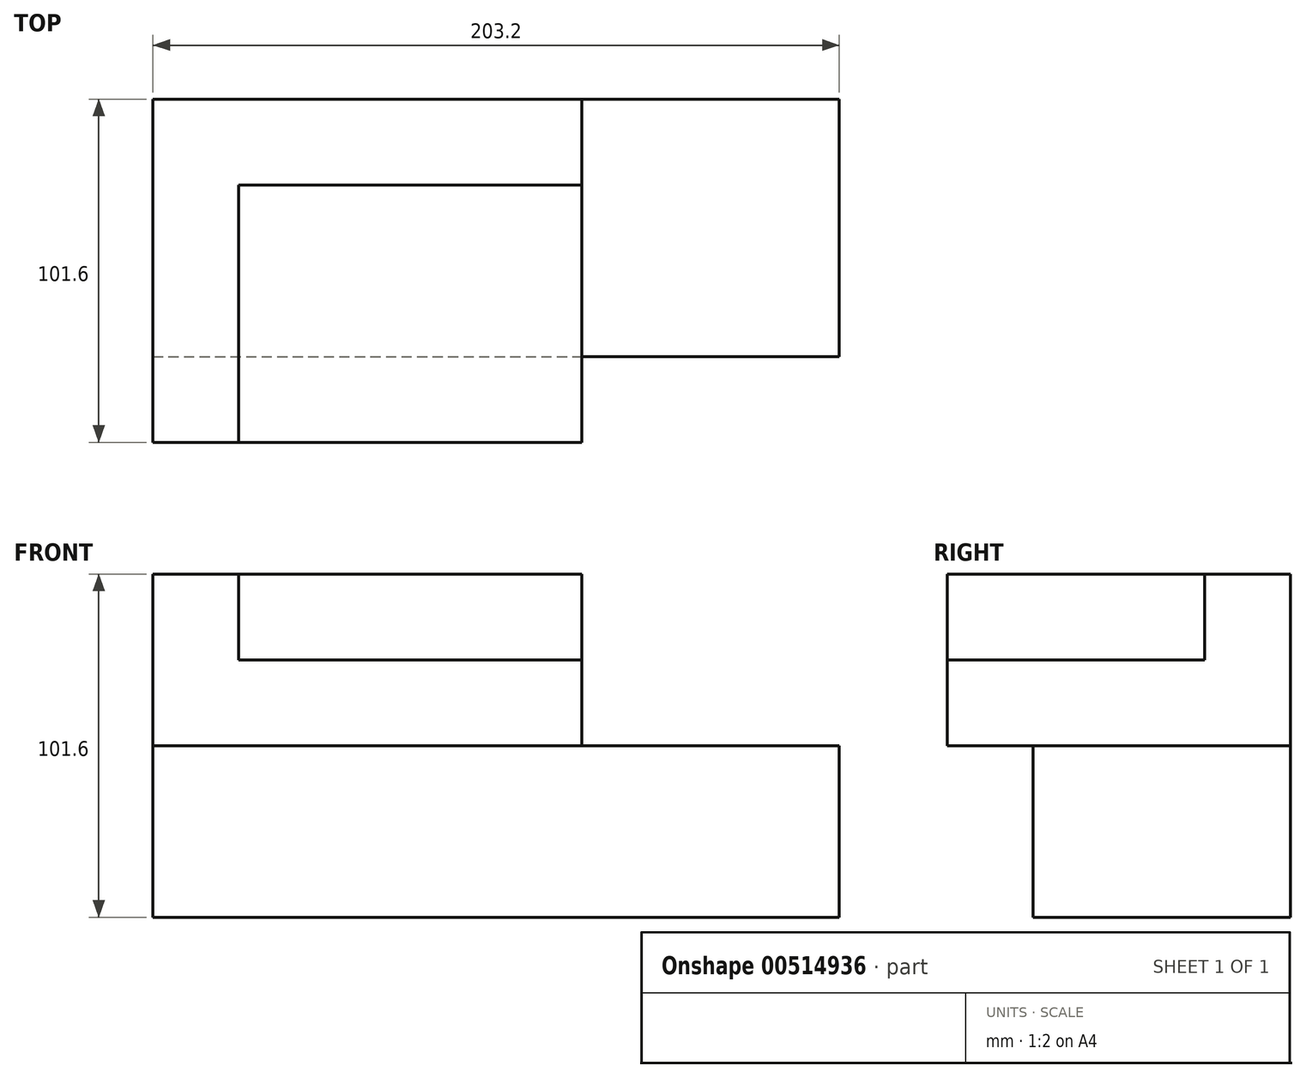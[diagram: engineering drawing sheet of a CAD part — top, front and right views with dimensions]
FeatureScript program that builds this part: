
annotation { "Feature Type Name" : "Feature", "Feature Type Description" : "" }
export const myFeature = defineFeature(function(context is Context, id is Id, definition is map)
    precondition{}
    {
        {
            var Q0;
            Q0=qCreatedBy(makeId("Top.planeOp"),FACE);
            var sketch = newSketch(context, id + "F0", { "sketchPlane" : qUnion([Q0])});
            skLineSegment(sketch, "E0.bottom", {"start": v(-101.35, 44.58) * mm, "end": v(101.85, 44.58) * mm});
            skLineSegment(sketch, "E0.top", {"start": v(-101.35, -57.02) * mm, "end": v(101.85, -57.02) * mm});
            skLineSegment(sketch, "E0.left", {"start": v(-101.35, 44.58) * mm, "end": v(-101.35, -57.02) * mm});
            skLineSegment(sketch, "E0.right", {"start": v(101.85, 44.58) * mm, "end": v(101.85, -57.02) * mm});
            skSolve(sketch);
        }
        {
            var Q0;
            Q0 = qSketchRegion(id + "F0", true);
            extrude(context, id + "F1", {"entities" : qUnion([Q0]), "depth" : 101.6 * mm, "offsetDistance" : 25.4 * mm});
        }
        {
            var Q0;
            Q0=makeQuery(id+"F1.opExtrude","SWEPT_FACE",FACE,{"disambiguationData":[OSD([sQuery(id+"F0.wireOp",EDGE,"E0.top")])]});
            var sketch = newSketch(context, id + "F2", { "sketchPlane" : qUnion([Q0])});
            skLineSegment(sketch, "E1.bottom", {"start": v(-101.35, 50.8) * mm, "end": v(101.85, 50.8) * mm});
            skLineSegment(sketch, "E1.top", {"start": v(-101.35, 0) * mm, "end": v(101.85, 0) * mm});
            skLineSegment(sketch, "E1.left", {"start": v(-101.35, 50.8) * mm, "end": v(-101.35, 0) * mm});
            skLineSegment(sketch, "E1.right", {"start": v(101.85, 50.8) * mm, "end": v(101.85, 0) * mm});
            skSolve(sketch);
        }
        {
            var Q0;
            Q0=makeQuery(id+"F2.imprint","IMPRINT",FACE,{"disambiguationData":[TD([[makeQuery(id+"F2.imprint","IMPRINT",EDGE,{"derivedFrom":sQuery(id+"F2.wireOp",EDGE,"E1.bottom")}),-1.0]])]});
            extrude(context, id + "F3", {"entities" : qUnion([Q0]), "operationType" : NewBodyOperationType.REMOVE, "oppositeDirection" : true, "depth" : 25.4 * mm, "offsetDistance" : 25.4 * mm});
        }
        {
            var Q0;
            Q0=makeQuery(id+"F1.opExtrude","CAP_FACE",FACE,{"disambiguationData":[OSD([sQuery(id+"F0.wireOp",EDGE,"E0.bottom"),sQuery(id+"F0.wireOp",EDGE,"E0.top"),sQuery(id+"F0.wireOp",EDGE,"E0.left"),sQuery(id+"F0.wireOp",EDGE,"E0.right")])],"isStart":false});
            var sketch = newSketch(context, id + "F4", { "sketchPlane" : qUnion([Q0])});
            skLineSegment(sketch, "E2.bottom", {"start": v(25.65, 44.58) * mm, "end": v(101.85, 44.58) * mm});
            skLineSegment(sketch, "E2.top", {"start": v(25.65, -57.02) * mm, "end": v(101.85, -57.02) * mm});
            skLineSegment(sketch, "E2.left", {"start": v(25.65, 44.58) * mm, "end": v(25.65, -57.02) * mm});
            skLineSegment(sketch, "E2.right", {"start": v(101.85, 44.58) * mm, "end": v(101.85, -57.02) * mm});
            skSolve(sketch);
        }
        {
            var Q0;
            Q0 = qSketchRegion(id + "F4", true);
            extrude(context, id + "F5", {"entities" : qUnion([Q0]), "operationType" : NewBodyOperationType.REMOVE, "oppositeDirection" : true, "depth" : 50.8 * mm, "offsetDistance" : 25.4 * mm});
        }
        {
            var Q0;
            Q0=makeQuery(id+"F1.opExtrude","CAP_FACE",FACE,{"disambiguationData":[OSD([sQuery(id+"F0.wireOp",EDGE,"E0.bottom"),sQuery(id+"F0.wireOp",EDGE,"E0.top"),sQuery(id+"F0.wireOp",EDGE,"E0.left"),sQuery(id+"F0.wireOp",EDGE,"E0.right")])],"isStart":false});
            var sketch = newSketch(context, id + "F6", { "sketchPlane" : qUnion([Q0])});
            skLineSegment(sketch, "E3.bottom", {"start": v(25.65, -57.02) * mm, "end": v(-75.95, -57.02) * mm});
            skLineSegment(sketch, "E3.top", {"start": v(25.65, 19.18) * mm, "end": v(-75.95, 19.18) * mm});
            skLineSegment(sketch, "E3.left", {"start": v(25.65, -57.02) * mm, "end": v(25.65, 19.18) * mm});
            skLineSegment(sketch, "E3.right", {"start": v(-75.95, -57.02) * mm, "end": v(-75.95, 19.18) * mm});
            skSolve(sketch);
        }
        {
            var Q0;
            Q0 = qSketchRegion(id + "F6", true);
            extrude(context, id + "F7", {"entities" : qUnion([Q0]), "operationType" : NewBodyOperationType.REMOVE, "oppositeDirection" : true, "depth" : 25.4 * mm, "offsetDistance" : 25.4 * mm});
        }
    });
